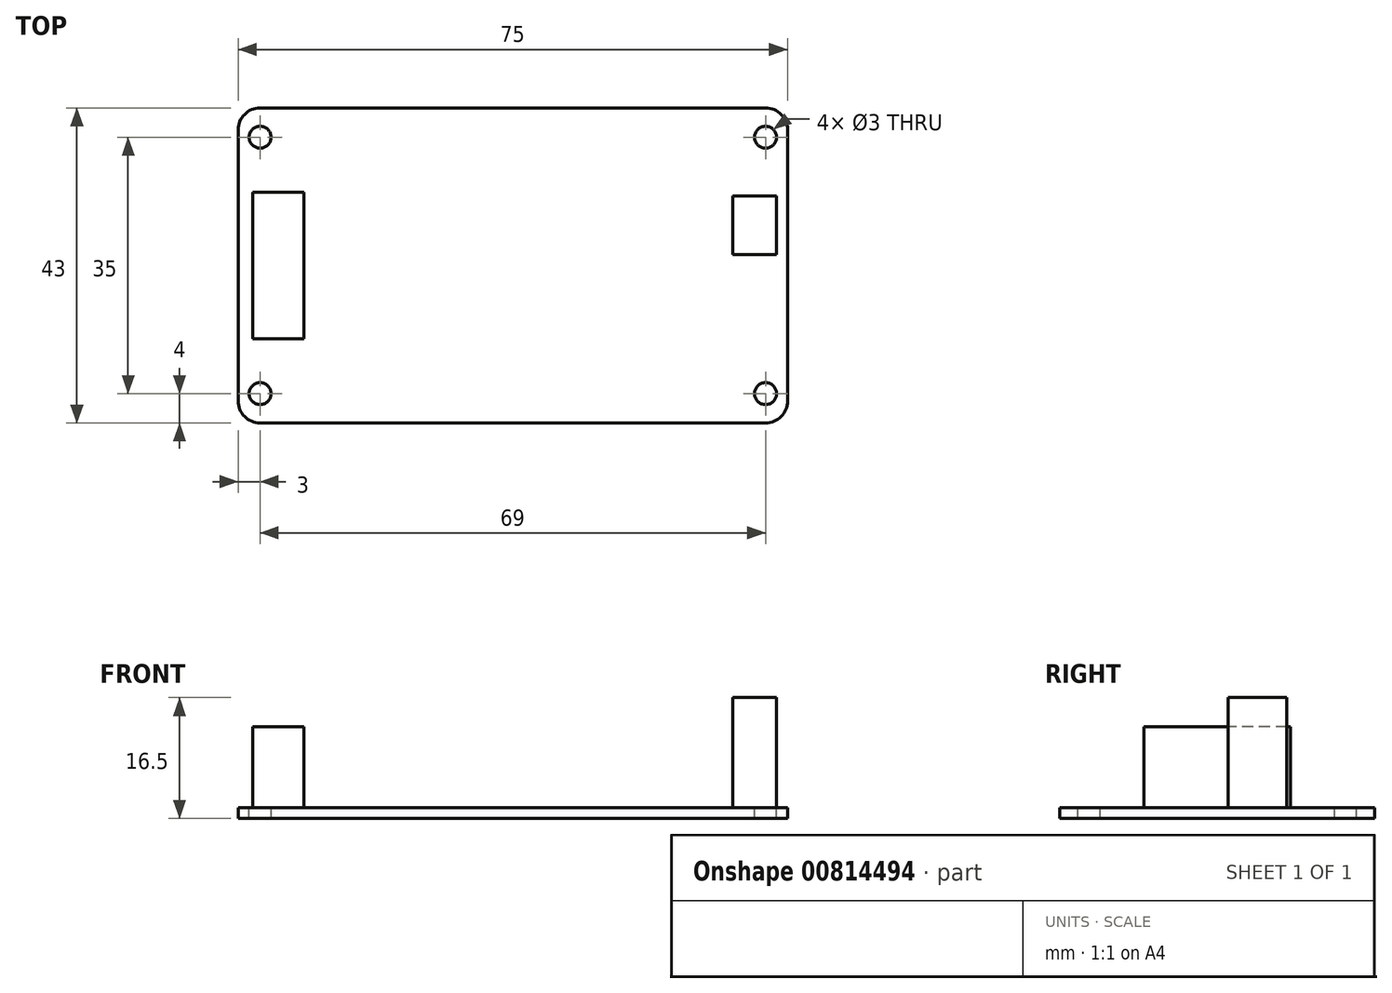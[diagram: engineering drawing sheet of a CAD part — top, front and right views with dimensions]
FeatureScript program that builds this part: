
annotation { "Feature Type Name" : "Feature", "Feature Type Description" : "" }
export const myFeature = defineFeature(function(context is Context, id is Id, definition is map)
    precondition{}
    {
        {
            var Q0;
            Q0=qCreatedBy(makeId("Top.planeOp"),FACE);
            var sketch = newSketch(context, id + "F0", { "sketchPlane" : qUnion([Q0])});
            skLineSegment(sketch, "E0.bottom", {"start": v(-37.5, -21.5) * mm, "end": v(37.5, -21.5) * mm});
            skLineSegment(sketch, "E0.top", {"start": v(-37.5, 21.5) * mm, "end": v(37.5, 21.5) * mm});
            skLineSegment(sketch, "E0.left", {"start": v(-37.5, -21.5) * mm, "end": v(-37.5, 21.5) * mm});
            skLineSegment(sketch, "E0.right", {"start": v(37.5, -21.5) * mm, "end": v(37.5, 21.5) * mm});
            skSolve(sketch);
        }
        {
            var Q0;
            Q0 = qSketchRegion(id + "F0", true);
            extrude(context, id + "F1", {"entities" : qUnion([Q0]), "depth" : 1.5 * mm, "offsetDistance" : 25 * mm});
        }
        {
            var Q0;
            Q0=makeQuery(id+"F1.opExtrude","CAP_FACE",FACE,{"disambiguationData":[OSD([sQuery(id+"F0.wireOp",EDGE,"E0.bottom"),sQuery(id+"F0.wireOp",EDGE,"E0.top"),sQuery(id+"F0.wireOp",EDGE,"E0.left"),sQuery(id+"F0.wireOp",EDGE,"E0.right")])],"isStart":false});
            var sketch = newSketch(context, id + "F2", { "sketchPlane" : qUnion([Q0])});
            skPoint(sketch, "E1", {"position": v(-34.5, 17.5) * mm});
            skPoint(sketch, "E2", {"position": v(34.5, 17.5) * mm});
            skPoint(sketch, "E3", {"position": v(34.5, -17.5) * mm});
            skPoint(sketch, "E4", {"position": v(-34.5, -17.5) * mm});
            skSolve(sketch);
        }
        {
            var Q0;
            Q0=sQuery(id+"F2.wireOp",VERTEX,"E1");
            var Q1;
            Q1=sQuery(id+"F2.wireOp",VERTEX,"E2");
            var Q2;
            Q2=sQuery(id+"F2.wireOp",VERTEX,"E3");
            var Q3;
            Q3=sQuery(id+"F2.wireOp",VERTEX,"E4");
            var Q4;
            Q4=makeQuery(id+"F1.opExtrude","SWEPT_BODY",BODY,{"disambiguationData":[OSD([sQuery(id+"F0.wireOp",EDGE,"E0.bottom"),sQuery(id+"F0.wireOp",EDGE,"E0.top"),sQuery(id+"F0.wireOp",EDGE,"E0.left"),sQuery(id+"F0.wireOp",EDGE,"E0.right")])]});
            hole(context, id + "F3", {"style" : HoleStyle.SIMPLE, "endStyle" : HoleEndStyle.THROUGH, "holeDiameter" : 3 * mm, "majorDiameter" : 5 * mm, "isTappedThrough" : true, "tappedDepth" : 12 * mm, "tapClearance" : 3, "locations" : qUnion([Q0, Q1, Q2, Q3]), "scope" : qUnion([Q4])});
        }
        {
            var Q0;
            Q0=makeQuery(id+"F1.opExtrude","SWEPT_EDGE",EDGE,{"disambiguationData":[OSD([sQuery(id+"F0.wireOp",EDGE,"E0.bottom"),sQuery(id+"F0.wireOp",EDGE,"E0.left")])]});
            var Q1;
            Q1=makeQuery(id+"F1.opExtrude","SWEPT_EDGE",EDGE,{"disambiguationData":[OSD([sQuery(id+"F0.wireOp",EDGE,"E0.bottom"),sQuery(id+"F0.wireOp",EDGE,"E0.right")])]});
            var Q2;
            Q2=makeQuery(id+"F1.opExtrude","SWEPT_EDGE",EDGE,{"disambiguationData":[OSD([sQuery(id+"F0.wireOp",EDGE,"E0.top"),sQuery(id+"F0.wireOp",EDGE,"E0.left")])]});
            var Q3;
            Q3=makeQuery(id+"F1.opExtrude","SWEPT_EDGE",EDGE,{"disambiguationData":[OSD([sQuery(id+"F0.wireOp",EDGE,"E0.top"),sQuery(id+"F0.wireOp",EDGE,"E0.right")])]});
            fillet(context, id + "F4", {"entities" : qUnion([Q0, Q1, Q2, Q3]), "radius" : 3 * mm, "tangentPropagation" : true, "allowEdgeOverflow" : false});
        }
        {
            var Q0;
            Q0=makeQuery(id+"F1.opExtrude","CAP_FACE",FACE,{"disambiguationData":[OSD([sQuery(id+"F0.wireOp",EDGE,"E0.bottom"),sQuery(id+"F0.wireOp",EDGE,"E0.top"),sQuery(id+"F0.wireOp",EDGE,"E0.left"),sQuery(id+"F0.wireOp",EDGE,"E0.right")])],"isStart":false});
            var sketch = newSketch(context, id + "F5", { "sketchPlane" : qUnion([Q0])});
            skLineSegment(sketch, "E5.bottom", {"start": v(-35.5, 10) * mm, "end": v(-28.5, 10) * mm});
            skLineSegment(sketch, "E5.top", {"start": v(-35.5, -10) * mm, "end": v(-28.5, -10) * mm});
            skLineSegment(sketch, "E5.left", {"start": v(-35.5, 10) * mm, "end": v(-35.5, -10) * mm});
            skLineSegment(sketch, "E5.right", {"start": v(-28.5, 10) * mm, "end": v(-28.5, -10) * mm});
            skSolve(sketch);
        }
        {
            var Q0;
            Q0 = qSketchRegion(id + "F5", true);
            extrude(context, id + "F6", {"entities" : qUnion([Q0]), "operationType" : NewBodyOperationType.ADD, "depth" : 11 * mm, "offsetDistance" : 25 * mm});
        }
        {
            var Q0;
            Q0=makeQuery(id+"F1.opExtrude","CAP_FACE",FACE,{"disambiguationData":[OSD([sQuery(id+"F0.wireOp",EDGE,"E0.bottom"),sQuery(id+"F0.wireOp",EDGE,"E0.top"),sQuery(id+"F0.wireOp",EDGE,"E0.left"),sQuery(id+"F0.wireOp",EDGE,"E0.right")])],"isStart":false});
            var sketch = newSketch(context, id + "F7", { "sketchPlane" : qUnion([Q0])});
            skLineSegment(sketch, "E6.bottom", {"start": v(30, 9.5) * mm, "end": v(36, 9.5) * mm});
            skLineSegment(sketch, "E6.top", {"start": v(30, 1.5) * mm, "end": v(36, 1.5) * mm});
            skLineSegment(sketch, "E6.left", {"start": v(30, 9.5) * mm, "end": v(30, 1.5) * mm});
            skLineSegment(sketch, "E6.right", {"start": v(36, 9.5) * mm, "end": v(36, 1.5) * mm});
            skSolve(sketch);
        }
        {
            var Q0;
            Q0 = qSketchRegion(id + "F7", true);
            extrude(context, id + "F8", {"entities" : qUnion([Q0]), "operationType" : NewBodyOperationType.ADD, "depth" : 15 * mm, "offsetDistance" : 25 * mm});
        }
    });
